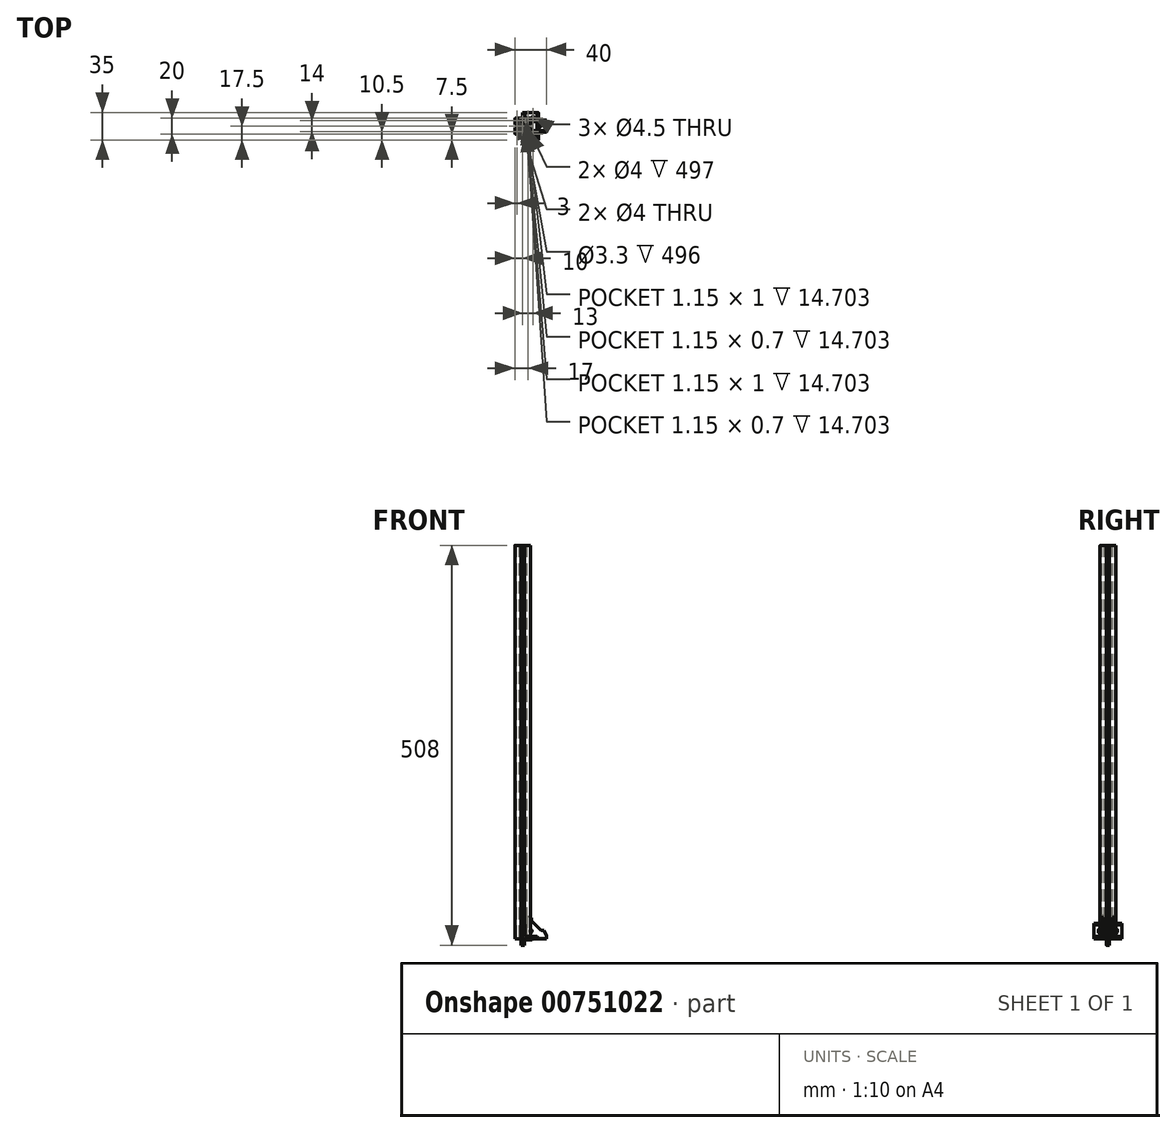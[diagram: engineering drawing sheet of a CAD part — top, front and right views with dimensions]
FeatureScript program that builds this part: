
annotation { "Feature Type Name" : "Feature", "Feature Type Description" : "" }
export const myFeature = defineFeature(function(context is Context, id is Id, definition is map)
    precondition{}
    {
        {
            var Q0;
            Q0=qCreatedBy(makeId("Top.planeOp"),FACE);
            var sketch = newSketch(context, id + "F0", { "sketchPlane" : qUnion([Q0])});
            skLineSegment(sketch, "E0", {"start": v(-9.5, 10) * mm, "end": v(-2.15, 10) * mm});
            skLineSegment(sketch, "E1", {"start": v(-2.15, 10) * mm, "end": v(-2.15, 8.5) * mm});
            skLineSegment(sketch, "E2", {"start": v(-2.15, 8.5) * mm, "end": v(-4.15, 8.5) * mm});
            skLineSegment(sketch, "E3", {"start": v(-4.15, 8.5) * mm, "end": v(-4.15, 4.8) * mm});
            skLineSegment(sketch, "E4", {"start": v(-4.15, 4.8) * mm, "end": v(-2.15, 4.8) * mm});
            skLineSegment(sketch, "E5", {"start": v(-2.15, 4.8) * mm, "end": v(-2.15, 3) * mm});
            skLineSegment(sketch, "E6", {"start": v(-2.15, 3) * mm, "end": v(0, 3) * mm});
            skLineSegment(sketch, "E7", {"start": v(0, 3) * mm, "end": v(0, 0) * mm});
            skLineSegment(sketch, "E8", {"start": v(0, 0) * mm, "end": v(-10, 10) * mm});
            skLineSegment(sketch, "E9.MirrorCS", {"start": v(-10, 9.5) * mm, "end": v(-10, 2.15) * mm});
            skLineSegment(sketch, "E10.MirrorCS", {"start": v(-8.5, 2.15) * mm, "end": v(-8.5, 4.15) * mm});
            skLineSegment(sketch, "E11.MirrorCS", {"start": v(-4.8, 2.15) * mm, "end": v(-3, 2.15) * mm});
            skLineSegment(sketch, "E12.MirrorCS", {"start": v(-10, 2.15) * mm, "end": v(-8.5, 2.15) * mm});
            skLineSegment(sketch, "E13.MirrorCS", {"start": v(-3, 2.15) * mm, "end": v(-3, 0) * mm});
            skLineSegment(sketch, "E14.MirrorCS", {"start": v(-4.8, 4.15) * mm, "end": v(-4.8, 2.15) * mm});
            skLineSegment(sketch, "E15.MirrorCS", {"start": v(-8.5, 4.15) * mm, "end": v(-4.8, 4.15) * mm});
            skLineSegment(sketch, "E16.MirrorCS", {"start": v(-3, 0) * mm, "end": v(0, 0) * mm});
            skCircle(sketch, "E17", {"center": v(-7, 7) * mm, "radius": 2 * mm});
            skLineSegment(sketch, "E18.1.0", {"start": v(-2.15, -3) * mm, "end": v(0, -3) * mm});
            skCircle(sketch, "E18.1.1", {"center": v(-7, -7) * mm, "radius": 2 * mm});
            skLineSegment(sketch, "E18.1.2", {"start": v(-2.15, -10) * mm, "end": v(-2.15, -8.5) * mm});
            skLineSegment(sketch, "E18.1.3", {"start": v(-2.15, -4.8) * mm, "end": v(-2.15, -3) * mm});
            skLineSegment(sketch, "E18.1.4", {"start": v(-2.15, -8.5) * mm, "end": v(-4.15, -8.5) * mm});
            skLineSegment(sketch, "E18.1.5", {"start": v(-9.5, -10) * mm, "end": v(-2.15, -10) * mm});
            skLineSegment(sketch, "E18.1.6", {"start": v(0, 0) * mm, "end": v(-10, -10) * mm});
            skLineSegment(sketch, "E18.1.7", {"start": v(-3, -2.15) * mm, "end": v(-3, 0) * mm});
            skLineSegment(sketch, "E18.1.8", {"start": v(-4.8, -2.15) * mm, "end": v(-3, -2.15) * mm});
            skLineSegment(sketch, "E18.1.9", {"start": v(-4.8, -4.15) * mm, "end": v(-4.8, -2.15) * mm});
            skLineSegment(sketch, "E18.1.10", {"start": v(-8.5, -4.15) * mm, "end": v(-4.8, -4.15) * mm});
            skLineSegment(sketch, "E18.1.11", {"start": v(-8.5, -2.15) * mm, "end": v(-8.5, -4.15) * mm});
            skLineSegment(sketch, "E18.1.12", {"start": v(-10, -2.15) * mm, "end": v(-8.5, -2.15) * mm});
            skLineSegment(sketch, "E18.1.13", {"start": v(-10, -9.5) * mm, "end": v(-10, -2.15) * mm});
            skLineSegment(sketch, "E18.1.14", {"start": v(-4.15, -8.5) * mm, "end": v(-4.15, -4.8) * mm});
            skLineSegment(sketch, "E18.1.15", {"start": v(-4.15, -4.8) * mm, "end": v(-2.15, -4.8) * mm});
            skLineSegment(sketch, "E18.2.0", {"start": v(3, -2.15) * mm, "end": v(3, 0) * mm});
            skCircle(sketch, "E18.2.1", {"center": v(7, -7) * mm, "radius": 2 * mm});
            skLineSegment(sketch, "E18.2.2", {"start": v(10, -2.15) * mm, "end": v(8.5, -2.15) * mm});
            skLineSegment(sketch, "E18.2.3", {"start": v(4.8, -2.15) * mm, "end": v(3, -2.15) * mm});
            skLineSegment(sketch, "E18.2.4", {"start": v(8.5, -2.15) * mm, "end": v(8.5, -4.15) * mm});
            skLineSegment(sketch, "E18.2.5", {"start": v(10, -9.5) * mm, "end": v(10, -2.15) * mm});
            skLineSegment(sketch, "E18.2.6", {"start": v(0, 0) * mm, "end": v(10, -10) * mm});
            skLineSegment(sketch, "E18.2.7", {"start": v(2.15, -3) * mm, "end": v(0, -3) * mm});
            skLineSegment(sketch, "E18.2.8", {"start": v(2.15, -4.8) * mm, "end": v(2.15, -3) * mm});
            skLineSegment(sketch, "E18.2.9", {"start": v(4.15, -4.8) * mm, "end": v(2.15, -4.8) * mm});
            skLineSegment(sketch, "E18.2.10", {"start": v(4.15, -8.5) * mm, "end": v(4.15, -4.8) * mm});
            skLineSegment(sketch, "E18.2.11", {"start": v(2.15, -8.5) * mm, "end": v(4.15, -8.5) * mm});
            skLineSegment(sketch, "E18.2.12", {"start": v(2.15, -10) * mm, "end": v(2.15, -8.5) * mm});
            skLineSegment(sketch, "E18.2.13", {"start": v(9.5, -10) * mm, "end": v(2.15, -10) * mm});
            skLineSegment(sketch, "E18.2.14", {"start": v(8.5, -4.15) * mm, "end": v(4.8, -4.15) * mm});
            skLineSegment(sketch, "E18.2.15", {"start": v(4.8, -4.15) * mm, "end": v(4.8, -2.15) * mm});
            skLineSegment(sketch, "E18.3.0", {"start": v(2.15, 3) * mm, "end": v(0, 3) * mm});
            skCircle(sketch, "E18.3.1", {"center": v(7, 7) * mm, "radius": 2 * mm});
            skLineSegment(sketch, "E18.3.2", {"start": v(2.15, 10) * mm, "end": v(2.15, 8.5) * mm});
            skLineSegment(sketch, "E18.3.3", {"start": v(2.15, 4.8) * mm, "end": v(2.15, 3) * mm});
            skLineSegment(sketch, "E18.3.4", {"start": v(2.15, 8.5) * mm, "end": v(4.15, 8.5) * mm});
            skLineSegment(sketch, "E18.3.5", {"start": v(9.5, 10) * mm, "end": v(2.15, 10) * mm});
            skLineSegment(sketch, "E18.3.6", {"start": v(0, 0) * mm, "end": v(10, 10) * mm});
            skLineSegment(sketch, "E18.3.7", {"start": v(3, 2.15) * mm, "end": v(3, 0) * mm});
            skLineSegment(sketch, "E18.3.8", {"start": v(4.8, 2.15) * mm, "end": v(3, 2.15) * mm});
            skLineSegment(sketch, "E18.3.9", {"start": v(4.8, 4.15) * mm, "end": v(4.8, 2.15) * mm});
            skLineSegment(sketch, "E18.3.10", {"start": v(8.5, 4.15) * mm, "end": v(4.8, 4.15) * mm});
            skLineSegment(sketch, "E18.3.11", {"start": v(8.5, 2.15) * mm, "end": v(8.5, 4.15) * mm});
            skLineSegment(sketch, "E18.3.12", {"start": v(10, 2.15) * mm, "end": v(8.5, 2.15) * mm});
            skLineSegment(sketch, "E18.3.13", {"start": v(10, 9.5) * mm, "end": v(10, 2.15) * mm});
            skLineSegment(sketch, "E18.3.14", {"start": v(4.15, 8.5) * mm, "end": v(4.15, 4.8) * mm});
            skLineSegment(sketch, "E18.3.15", {"start": v(4.15, 4.8) * mm, "end": v(2.15, 4.8) * mm});
            skPoint(sketch, "E18.center", {"position": v(0, 0) * mm});
            skCircle(sketch, "E19", {"center": v(0, 0) * mm, "radius": 1.65 * mm});
            skPoint(sketch, "E20.visualSharp", {"position": v(-10, 10) * mm});
            skArc(sketch, "E20.filletArc", {"start": v(-9.5, 10) * mm, "mid": v(-9.85, 9.85) * mm, "end": v(-10, 9.5) * mm});
            skPoint(sketch, "E21.visualSharp", {"position": v(10, 10) * mm});
            skArc(sketch, "E21.filletArc", {"start": v(10, 9.5) * mm, "mid": v(9.85, 9.85) * mm, "end": v(9.5, 10) * mm});
            skPoint(sketch, "E22.visualSharp", {"position": v(10, -10) * mm});
            skArc(sketch, "E22.filletArc", {"start": v(9.5, -10) * mm, "mid": v(9.85, -9.85) * mm, "end": v(10, -9.5) * mm});
            skPoint(sketch, "E23.visualSharp", {"position": v(-10, -10) * mm});
            skArc(sketch, "E23.filletArc", {"start": v(-10, -9.5) * mm, "mid": v(-9.85, -9.85) * mm, "end": v(-9.5, -10) * mm});
            skSolve(sketch);
        }
        {
            var Q0;
            Q0=qSketchRegion(id+"F0",true);
            extrude(context, id + "F1", {"entities" : qUnion([Q0]), "depth" : 25 * mm});
        }
        {
            var Q0;
            Q0=qCreatedBy(makeId("Front.planeOp"),FACE);
            var sketch = newSketch(context, id + "F2", { "sketchPlane" : qUnion([Q0])});
            skLineSegment(sketch, "E24", {"start": v(0, 0) * mm, "end": v(30, 0) * mm});
            skLineSegment(sketch, "E25", {"start": v(30, 0) * mm, "end": v(30, 4) * mm});
            skLineSegment(sketch, "E26", {"start": v(30, 4) * mm, "end": v(27, 11) * mm});
            skLineSegment(sketch, "E27", {"start": v(27, 11) * mm, "end": v(23, 11) * mm});
            skLineSegment(sketch, "E28", {"start": v(23, 11) * mm, "end": v(17, 17) * mm});
            skLineSegment(sketch, "E29", {"start": v(0, 0) * mm, "end": v(17, 17) * mm});
            skLineSegment(sketch, "E30.MirrorCS", {"start": v(11, 23) * mm, "end": v(17, 17) * mm});
            skLineSegment(sketch, "E31.MirrorCS", {"start": v(0, 30) * mm, "end": v(4, 30) * mm});
            skLineSegment(sketch, "E32.MirrorCS", {"start": v(11, 27) * mm, "end": v(11, 23) * mm});
            skLineSegment(sketch, "E33.MirrorCS", {"start": v(4, 30) * mm, "end": v(11, 27) * mm});
            skLineSegment(sketch, "E34.MirrorCS", {"start": v(0, 0) * mm, "end": v(0, 30) * mm});
            skSolve(sketch);
        }
        {
            var Q0;
            Q0=qSketchRegion(id+"F2",true);
            extrude(context, id + "F3", {"entities" : qUnion([Q0]), "endBound" : BoundingType.SYMMETRIC, "depth" : 15 * mm});
        }
        {
            var Q0;
            Q0=makeQuery(id+"F3.opExtrude","SWEPT_FACE",FACE,{"disambiguationData":[OSD([sQuery(id+"F2.wireOp",EDGE,"E31.MirrorCS")])]});
            var Q1;
            Q1=makeQuery(id+"F3.opExtrude","SWEPT_FACE",FACE,{"disambiguationData":[OSD([sQuery(id+"F2.wireOp",EDGE,"E33.MirrorCS")])]});
            var Q2;
            Q2=makeQuery(id+"F3.opExtrude","SWEPT_FACE",FACE,{"disambiguationData":[OSD([sQuery(id+"F2.wireOp",EDGE,"E28"),sQuery(id+"F2.wireOp",EDGE,"E30.MirrorCS")])]});
            var Q3;
            Q3=makeQuery(id+"F3.opExtrude","SWEPT_FACE",FACE,{"disambiguationData":[OSD([sQuery(id+"F2.wireOp",EDGE,"E27")])]});
            var Q4;
            Q4=makeQuery(id+"F3.opExtrude","SWEPT_FACE",FACE,{"disambiguationData":[OSD([sQuery(id+"F2.wireOp",EDGE,"E26")])]});
            var Q5;
            Q5=makeQuery(id+"F3.opExtrude","SWEPT_FACE",FACE,{"disambiguationData":[OSD([sQuery(id+"F2.wireOp",EDGE,"E25")])]});
            var Q6;
            Q6=makeQuery(id+"F3.opExtrude","SWEPT_FACE",FACE,{"disambiguationData":[OSD([sQuery(id+"F2.wireOp",EDGE,"E32.MirrorCS")])]});
            shell(context, id + "F4", {"entities" : qUnion([Q0, Q1, Q2, Q3, Q4, Q5, Q6]), "thickness" : 2 * mm});
        }
        {
            var Q0;
            Q0=makeQuery(id+"F3.opExtrude","SWEPT_FACE",FACE,{"disambiguationData":[OSD([sQuery(id+"F2.wireOp",EDGE,"E34.MirrorCS")])]});
            var sketch = newSketch(context, id + "F5", { "sketchPlane" : qUnion([Q0])});
            skCircle(sketch, "E35", {"center": v(0, 20) * mm, "radius": 2.5 * mm});
            skSolve(sketch);
        }
        {
            var Q0;
            Q0=qSketchRegion(id+"F5",true);
            var Q1;
            Q1=makeQuery(id+"F4.opShell","OFFSET_FACE",FACE,{"disambiguationData":[OSD([sQuery(id+"F2.wireOp",EDGE,"E34.MirrorCS")])]});
            extrude(context, id + "F6", {"entities" : qUnion([Q0]), "operationType" : NewBodyOperationType.REMOVE, "endBound" : BoundingType.UP_TO_SURFACE, "oppositeDirection" : true, "endBoundEntityFace" : qUnion([Q1]), "depth" : 25 * mm});
        }
        {
            var Q0;
            Q0=makeQuery(id+"F3.opExtrude","SWEPT_FACE",FACE,{"disambiguationData":[OSD([sQuery(id+"F2.wireOp",EDGE,"E24")])]});
            var sketch = newSketch(context, id + "F7", { "sketchPlane" : qUnion([Q0])});
            skCircle(sketch, "E36", {"center": v(20, 0) * mm, "radius": 2.5 * mm});
            skSolve(sketch);
        }
        {
            var Q0;
            Q0=qSketchRegion(id+"F7",true);
            var Q1;
            Q1=makeQuery(id+"F4.opShell","OFFSET_FACE",FACE,{"disambiguationData":[OSD([sQuery(id+"F2.wireOp",EDGE,"E24")])]});
            extrude(context, id + "F8", {"entities" : qUnion([Q0]), "operationType" : NewBodyOperationType.REMOVE, "endBound" : BoundingType.UP_TO_SURFACE, "oppositeDirection" : true, "endBoundEntityFace" : qUnion([Q1]), "depth" : 25 * mm});
        }
        {
            var Q0;
            Q0=makeQuery(id+"F3.opExtrude","CAP_FACE",FACE,{"disambiguationData":[OSD([sQuery(id+"F2.wireOp",EDGE,"E24"),sQuery(id+"F2.wireOp",EDGE,"E25"),sQuery(id+"F2.wireOp",EDGE,"E26"),sQuery(id+"F2.wireOp",EDGE,"E27"),sQuery(id+"F2.wireOp",EDGE,"E28"),sQuery(id+"F2.wireOp",EDGE,"E30.MirrorCS"),sQuery(id+"F2.wireOp",EDGE,"E31.MirrorCS"),sQuery(id+"F2.wireOp",EDGE,"E32.MirrorCS"),sQuery(id+"F2.wireOp",EDGE,"E33.MirrorCS"),sQuery(id+"F2.wireOp",EDGE,"E34.MirrorCS")])],"isStart":false});
            var sketch = newSketch(context, id + "F9", { "sketchPlane" : qUnion([Q0])});
            skCircle(sketch, "E37", {"center": v(10, 10) * mm, "radius": 2 * mm});
            skSolve(sketch);
        }
        {
            var Q0;
            Q0=qSketchRegion(id+"F9",true);
            var Q1;
            {var subQ0=sQuery(id+"F2.wireOp",EDGE,"E24");var subQ1=sQuery(id+"F2.wireOp",EDGE,"E25");var subQ2=sQuery(id+"F2.wireOp",EDGE,"E26");var subQ3=sQuery(id+"F2.wireOp",EDGE,"E27");var subQ4=sQuery(id+"F2.wireOp",EDGE,"E28");var subQ5=sQuery(id+"F2.wireOp",EDGE,"E30.MirrorCS");var subQ6=sQuery(id+"F2.wireOp",EDGE,"E31.MirrorCS");var subQ7=sQuery(id+"F2.wireOp",EDGE,"E32.MirrorCS");var subQ8=sQuery(id+"F2.wireOp",EDGE,"E33.MirrorCS");var subQ9=sQuery(id+"F2.wireOp",EDGE,"E34.MirrorCS");Q1=makeQuery(id+"F4.opShell","OFFSET_FACE",FACE,{"disambiguationData":[OSD([subQ0,subQ1,subQ2,subQ3,subQ4,subQ5,subQ6,subQ7,subQ8,subQ9]),TDD([makeQuery(id+"F3.opExtrude","CAP_FACE",FACE,{"disambiguationData":[OSD([subQ0,subQ1,subQ2,subQ3,subQ4,subQ5,subQ6,subQ7,subQ8,subQ9])],"isStart":true})])]});}
            extrude(context, id + "F10", {"entities" : qUnion([Q0]), "operationType" : NewBodyOperationType.REMOVE, "endBound" : BoundingType.UP_TO_SURFACE, "oppositeDirection" : true, "endBoundEntityFace" : qUnion([Q1]), "depth" : 25 * mm});
        }
        {
            var Q0;
            Q0=qCreatedBy(makeId("Front.planeOp"),FACE);
            var sketch = newSketch(context, id + "F11", { "sketchPlane" : qUnion([Q0])});
            skLineSegment(sketch, "E38", {"start": v(0, 13) * mm, "end": v(-1.5, 11.5) * mm});
            skLineSegment(sketch, "E39", {"start": v(-1.5, 11.5) * mm, "end": v(-1.5, 1.5) * mm});
            skLineSegment(sketch, "E40", {"start": v(-1.5, 1.5) * mm, "end": v(0, 0) * mm});
            skLineSegment(sketch, "E41", {"start": v(0, 0) * mm, "end": v(1.5, -1.5) * mm});
            skLineSegment(sketch, "E42", {"start": v(1.5, -1.5) * mm, "end": v(11.5, -1.5) * mm});
            skLineSegment(sketch, "E43", {"start": v(11.5, -1.5) * mm, "end": v(13, 0) * mm});
            skLineSegment(sketch, "E44", {"start": v(13, 0) * mm, "end": v(0, 0) * mm});
            skLineSegment(sketch, "E45", {"start": v(0, 13) * mm, "end": v(0, 0) * mm});
            skSolve(sketch);
        }
        {
            var Q0;
            Q0=qSketchRegion(id+"F11",true);
            extrude(context, id + "F12", {"entities" : qUnion([Q0]), "operationType" : NewBodyOperationType.ADD, "endBound" : BoundingType.SYMMETRIC, "depth" : 4 * mm});
        }
        {
            var Q0;
            Q0=qSketchRegion(id+"F11",true);
            extrude(context, id + "F13", {"entities" : qUnion([Q0]), "operationType" : NewBodyOperationType.REMOVE, "endBound" : BoundingType.SYMMETRIC, "oppositeDirection" : true, "depth" : 1 * mm});
        }
        {
            var Q0;
            Q0=qCreatedBy(makeId("Front.planeOp"),FACE);
            var sketch = newSketch(context, id + "F14", { "sketchPlane" : qUnion([Q0])});
            skLineSegment(sketch, "E46", {"start": v(0, 20) * mm, "end": v(0, 0) * mm});
            skLineSegment(sketch, "E47", {"start": v(0, 0) * mm, "end": v(20, 0) * mm});
            skLineSegment(sketch, "E48", {"start": v(18.08, 3) * mm, "end": v(3, 3) * mm});
            skLineSegment(sketch, "E49", {"start": v(3, 3) * mm, "end": v(3, 17.7) * mm});
            skArc(sketch, "E50", {"start": v(20, 0) * mm, "mid": v(19.48, 1.78) * mm, "end": v(18.08, 3) * mm});
            skArc(sketch, "E51", {"start": v(3, 17.7) * mm, "mid": v(1.89, 19.36) * mm, "end": v(0, 20) * mm});
            skSolve(sketch);
        }
        {
            var Q0;
            Q0=qSketchRegion(id+"F14",true);
            extrude(context, id + "F15", {"entities" : qUnion([Q0]), "endBound" : BoundingType.SYMMETRIC, "depth" : 15 * mm});
        }
        {
            var Q0;
            Q0=makeQuery(id+"F15.opExtrude","SWEPT_FACE",FACE,{"disambiguationData":[OSD([sQuery(id+"F14.wireOp",EDGE,"E48")])]});
            var sketch = newSketch(context, id + "F16", { "sketchPlane" : qUnion([Q0])});
            skCircle(sketch, "E52", {"center": v(13, 0) * mm, "radius": 2.25 * mm});
            skSolve(sketch);
        }
        {
            var Q0;
            Q0=qSketchRegion(id+"F16",true);
            var Q1;
            Q1=makeQuery(id+"F15.opExtrude","SWEPT_FACE",FACE,{"disambiguationData":[OSD([sQuery(id+"F14.wireOp",EDGE,"E47")])]});
            extrude(context, id + "F17", {"entities" : qUnion([Q0]), "operationType" : NewBodyOperationType.REMOVE, "endBound" : BoundingType.UP_TO_SURFACE, "oppositeDirection" : true, "endBoundEntityFace" : qUnion([Q1]), "depth" : 25 * mm});
        }
        {
            var Q0;
            Q0=makeQuery(id+"F15.opExtrude","SWEPT_FACE",FACE,{"disambiguationData":[OSD([sQuery(id+"F14.wireOp",EDGE,"E46")])]});
            var sketch = newSketch(context, id + "F18", { "sketchPlane" : qUnion([Q0])});
            skLineSegment(sketch, "E53.rect.left", {"start": v(2.25, 9.25) * mm, "end": v(2.25, 10.75) * mm});
            skLineSegment(sketch, "E53.rect.right", {"start": v(-2.25, 9.25) * mm, "end": v(-2.25, 10.75) * mm});
            skPoint(sketch, "E53.rect.middle", {"position": v(0, 10) * mm});
            skArc(sketch, "E54", {"start": v(2.25, 10.75) * mm, "mid": v(0, 13) * mm, "end": v(-2.25, 10.75) * mm});
            skArc(sketch, "E55", {"start": v(-2.25, 9.25) * mm, "mid": v(0, 7) * mm, "end": v(2.25, 9.25) * mm});
            skSolve(sketch);
        }
        {
            var Q0;
            Q0=qSketchRegion(id+"F18",true);
            var Q1;
            Q1=makeQuery(id+"F15.opExtrude","SWEPT_FACE",FACE,{"disambiguationData":[OSD([sQuery(id+"F14.wireOp",EDGE,"E49")])]});
            extrude(context, id + "F19", {"entities" : qUnion([Q0]), "operationType" : NewBodyOperationType.REMOVE, "endBound" : BoundingType.UP_TO_SURFACE, "oppositeDirection" : true, "endBoundEntityFace" : qUnion([Q1]), "depth" : 25 * mm});
        }
        {
            var Q0;
            Q0=qSketchRegion(id+"F14",true);
            extrude(context, id + "F20", {"entities" : qUnion([Q0]), "endBound" : BoundingType.SYMMETRIC, "depth" : 35 * mm});
        }
        {
            var Q0;
            Q0=makeQuery(id+"F20.opExtrude","SWEPT_FACE",FACE,{"disambiguationData":[OSD([sQuery(id+"F14.wireOp",EDGE,"E48")])]});
            var sketch = newSketch(context, id + "F21", { "sketchPlane" : qUnion([Q0])});
            skLineSegment(sketch, "E56", {"start": v(5.7, 0) * mm, "end": v(16.15, 0) * mm, "construction": true});
            skCircle(sketch, "E57", {"center": v(13, -10) * mm, "radius": 2.25 * mm});
            skCircle(sketch, "E58.MirrorC", {"center": v(13, 10) * mm, "radius": 2.25 * mm});
            skSolve(sketch);
        }
        {
            var Q0;
            Q0=qSketchRegion(id+"F21",true);
            var Q1;
            Q1=makeQuery(id+"F20.opExtrude","SWEPT_FACE",FACE,{"disambiguationData":[OSD([sQuery(id+"F14.wireOp",EDGE,"E47")])]});
            extrude(context, id + "F22", {"entities" : qUnion([Q0]), "operationType" : NewBodyOperationType.REMOVE, "endBound" : BoundingType.UP_TO_SURFACE, "oppositeDirection" : true, "endBoundEntityFace" : qUnion([Q1]), "depth" : 25 * mm});
        }
        {
            var Q0;
            Q0=makeQuery(id+"F20.opExtrude","SWEPT_FACE",FACE,{"disambiguationData":[OSD([sQuery(id+"F14.wireOp",EDGE,"E49")])]});
            var sketch = newSketch(context, id + "F23", { "sketchPlane" : qUnion([Q0])});
            skLineSegment(sketch, "E59", {"start": v(0, 13.28) * mm, "end": v(0, 4.05) * mm, "construction": true});
            skLineSegment(sketch, "E60.rect.left", {"start": v(-7.75, 9.25) * mm, "end": v(-7.75, 10.75) * mm});
            skLineSegment(sketch, "E60.rect.right", {"start": v(-12.25, 9.25) * mm, "end": v(-12.25, 10.75) * mm});
            skPoint(sketch, "E60.rect.middle", {"position": v(-10, 10) * mm});
            skArc(sketch, "E61", {"start": v(-7.75, 10.75) * mm, "mid": v(-10, 13) * mm, "end": v(-12.25, 10.75) * mm});
            skArc(sketch, "E62", {"start": v(-12.25, 9.25) * mm, "mid": v(-10, 7) * mm, "end": v(-7.75, 9.25) * mm});
            skLineSegment(sketch, "E63", {"start": v(-10, 10) * mm, "end": v(-10, 13.42) * mm, "construction": true});
            skLineSegment(sketch, "E64.MirrorCS", {"start": v(12.25, 9.25) * mm, "end": v(12.25, 10.75) * mm});
            skLineSegment(sketch, "E65.MirrorCS", {"start": v(7.75, 9.25) * mm, "end": v(7.75, 10.75) * mm});
            skPoint(sketch, "E66.MirrorP", {"position": v(10, 10) * mm});
            skArc(sketch, "E67.MirrorCS", {"start": v(12.25, 9.25) * mm, "mid": v(10, 7) * mm, "end": v(7.75, 9.25) * mm});
            skArc(sketch, "E68.MirrorCS", {"start": v(7.75, 10.75) * mm, "mid": v(10, 13) * mm, "end": v(12.25, 10.75) * mm});
            skSolve(sketch);
        }
        {
            var Q0;
            Q0=qSketchRegion(id+"F23",true);
            var Q1;
            Q1=makeQuery(id+"F20.opExtrude","SWEPT_FACE",FACE,{"disambiguationData":[OSD([sQuery(id+"F14.wireOp",EDGE,"E46")])]});
            extrude(context, id + "F24", {"entities" : qUnion([Q0]), "operationType" : NewBodyOperationType.REMOVE, "endBound" : BoundingType.UP_TO_SURFACE, "oppositeDirection" : true, "endBoundEntityFace" : qUnion([Q1]), "depth" : 25 * mm});
        }
        {
            var Q0;
            Q0=qCreatedBy(makeId("Top.planeOp"),FACE);
            var sketch = newSketch(context, id + "F25", { "sketchPlane" : qUnion([Q0])});
            skLineSegment(sketch, "E69.rect.bottom", {"start": v(4, -4) * mm, "end": v(-4, -4) * mm});
            skLineSegment(sketch, "E69.rect.top", {"start": v(4, 4) * mm, "end": v(-4, 4) * mm});
            skLineSegment(sketch, "E69.rect.left", {"start": v(4, -4) * mm, "end": v(4, 4) * mm});
            skLineSegment(sketch, "E69.rect.right", {"start": v(-4, -4) * mm, "end": v(-4, 4) * mm});
            skPoint(sketch, "E69.rect.middle", {"position": v(0, 0) * mm});
            skCircle(sketch, "E70", {"center": v(0, 0) * mm, "radius": 2 * mm});
            skSolve(sketch);
        }
        {
            var Q0;
            Q0=qSketchRegion(id+"F25",true);
            extrude(context, id + "F26", {"entities" : qUnion([Q0]), "depth" : 3.2 * mm});
        }
        {
            var Q0;
            Q0=qCreatedBy(makeId("Top.planeOp"),FACE);
            var sketch = newSketch(context, id + "F27", { "sketchPlane" : qUnion([Q0])});
            skLineSegment(sketch, "E71.rect.bottom", {"start": v(4, -4) * mm, "end": v(-4, -4) * mm});
            skLineSegment(sketch, "E71.rect.top", {"start": v(4, 4) * mm, "end": v(-4, 4) * mm});
            skLineSegment(sketch, "E71.rect.left", {"start": v(4, -4) * mm, "end": v(4, 4) * mm});
            skLineSegment(sketch, "E71.rect.right", {"start": v(-4, -4) * mm, "end": v(-4, 4) * mm});
            skPoint(sketch, "E71.rect.middle", {"position": v(0, 0) * mm});
            skCircle(sketch, "E72", {"center": v(0, 0) * mm, "radius": 1.5 * mm});
            skSolve(sketch);
        }
        {
            var Q0;
            Q0=qSketchRegion(id+"F27",true);
            extrude(context, id + "F28", {"entities" : qUnion([Q0]), "depth" : 3.2 * mm});
        }
        {
            var Q0;
            Q0=qSketchRegion(id+"F0",true);
            extrude(context, id + "F29", {"entities" : qUnion([Q0]), "depth" : 500 * mm});
        }
        {
            var Q0;
            Q0=qSketchRegion(id+"F0",true);
            extrude(context, id + "F30", {"entities" : qUnion([Q0]), "depth" : 330 * mm});
        }
        {
            var Q0;
            Q0=qCreatedBy(makeId("Top.planeOp"),FACE);
            var sketch = newSketch(context, id + "F31", { "sketchPlane" : qUnion([Q0])});
            skCircle(sketch, "E73", {"center": v(0, 0) * mm, "radius": 3.5 * mm});
            skSolve(sketch);
        }
        {
            var Q0;
            Q0=qSketchRegion(id+"F31",true);
            extrude(context, id + "F32", {"entities" : qUnion([Q0]), "depth" : 4 * mm});
        }
        {
            var Q0;
            Q0=makeQuery(id+"F32.opExtrude","CAP_EDGE",EDGE,{"disambiguationData":[OSD([sQuery(id+"F31.wireOp",EDGE,"E73")])],"isStart":false});
            var Q1;
            Q1=makeQuery(id+"F32.opExtrude","CAP_EDGE",EDGE,{"disambiguationData":[OSD([sQuery(id+"F31.wireOp",EDGE,"E73")])],"isStart":true});
            fillet(context, id + "F33", {"entities" : qUnion([Q0, Q1]), "radius" : 0.5 * mm, "tangentPropagation" : true, "allowEdgeOverflow" : false});
        }
        {
            var Q0;
            Q0=makeQuery(id+"F32.opExtrude","CAP_FACE",FACE,{"disambiguationData":[OSD([sQuery(id+"F31.wireOp",EDGE,"E73")])],"isStart":false});
            var sketch = newSketch(context, id + "F34", { "sketchPlane" : qUnion([Q0])});
            skCircle(sketch, "E74.cCircle", {"center": v(0, 0) * mm, "radius": 1.5 * mm, "construction": true});
            skLineSegment(sketch, "E74.0", {"start": v(-0.87, 1.5) * mm, "end": v(0.87, 1.5) * mm});
            skLineSegment(sketch, "E74.1", {"start": v(0.87, 1.5) * mm, "end": v(1.73, 0) * mm});
            skLineSegment(sketch, "E74.2", {"start": v(1.73, 0) * mm, "end": v(0.87, -1.5) * mm});
            skLineSegment(sketch, "E74.3", {"start": v(0.87, -1.5) * mm, "end": v(-0.87, -1.5) * mm});
            skLineSegment(sketch, "E74.4", {"start": v(-0.87, -1.5) * mm, "end": v(-1.73, 0) * mm});
            skLineSegment(sketch, "E74.5", {"start": v(-1.73, 0) * mm, "end": v(-0.87, 1.5) * mm});
            skPoint(sketch, "E74.0.midPoint", {"position": v(0, 1.5) * mm});
            skSolve(sketch);
        }
        {
            var Q0;
            Q0=qSketchRegion(id+"F34",true);
            extrude(context, id + "F35", {"entities" : qUnion([Q0]), "operationType" : NewBodyOperationType.REMOVE, "oppositeDirection" : true, "depth" : 2 * mm});
        }
        {
            var Q0;
            Q0=makeQuery(id+"F32.opExtrude","CAP_FACE",FACE,{"disambiguationData":[OSD([sQuery(id+"F31.wireOp",EDGE,"E73")])],"isStart":true});
            var sketch = newSketch(context, id + "F36", { "sketchPlane" : qUnion([Q0])});
            skCircle(sketch, "E75", {"center": v(0, 0) * mm, "radius": 2 * mm});
            skSolve(sketch);
        }
        {
            var Q0;
            Q0=qSketchRegion(id+"F36",true);
            extrude(context, id + "F37", {"entities" : qUnion([Q0]), "operationType" : NewBodyOperationType.ADD, "depth" : 8 * mm});
        }
        {
            var Q0;
            Q0=qCreatedBy(makeId("Top.planeOp"),FACE);
            var sketch = newSketch(context, id + "F38", { "sketchPlane" : qUnion([Q0])});
            skCircle(sketch, "E76", {"center": v(0, 0) * mm, "radius": 5 * mm});
            skCircle(sketch, "E77", {"center": v(0, 0) * mm, "radius": 2.25 * mm});
            skSolve(sketch);
        }
        {
            var Q0;
            Q0=qSketchRegion(id+"F38",true);
            extrude(context, id + "F39", {"entities" : qUnion([Q0]), "depth" : 0.8 * mm});
        }
        {
            var Q0;
            Q0=qCreatedBy(makeId("Top.planeOp"),FACE);
            var sketch = newSketch(context, id + "F40", { "sketchPlane" : qUnion([Q0])});
            skArc(sketch, "E78", {"start": v(0.25, -3.8) * mm, "mid": v(0, 3.8) * mm, "end": v(-0.25, -3.8) * mm});
            skArc(sketch, "E79", {"start": v(0.25, -2.03) * mm, "mid": v(0, 2.05) * mm, "end": v(-0.25, -2.03) * mm});
            skLineSegment(sketch, "E80", {"start": v(0.25, -3.8) * mm, "end": v(0.25, -2.03) * mm});
            skLineSegment(sketch, "E81", {"start": v(0, 0) * mm, "end": v(0, -1.8) * mm, "construction": true});
            skLineSegment(sketch, "E82", {"start": v(-0.25, -3.8) * mm, "end": v(-0.25, -2.03) * mm});
            skSolve(sketch);
        }
        {
            var Q0;
            Q0=qSketchRegion(id+"F40",true);
            extrude(context, id + "F41", {"entities" : qUnion([Q0]), "depth" : 1 * mm});
        }
    });
